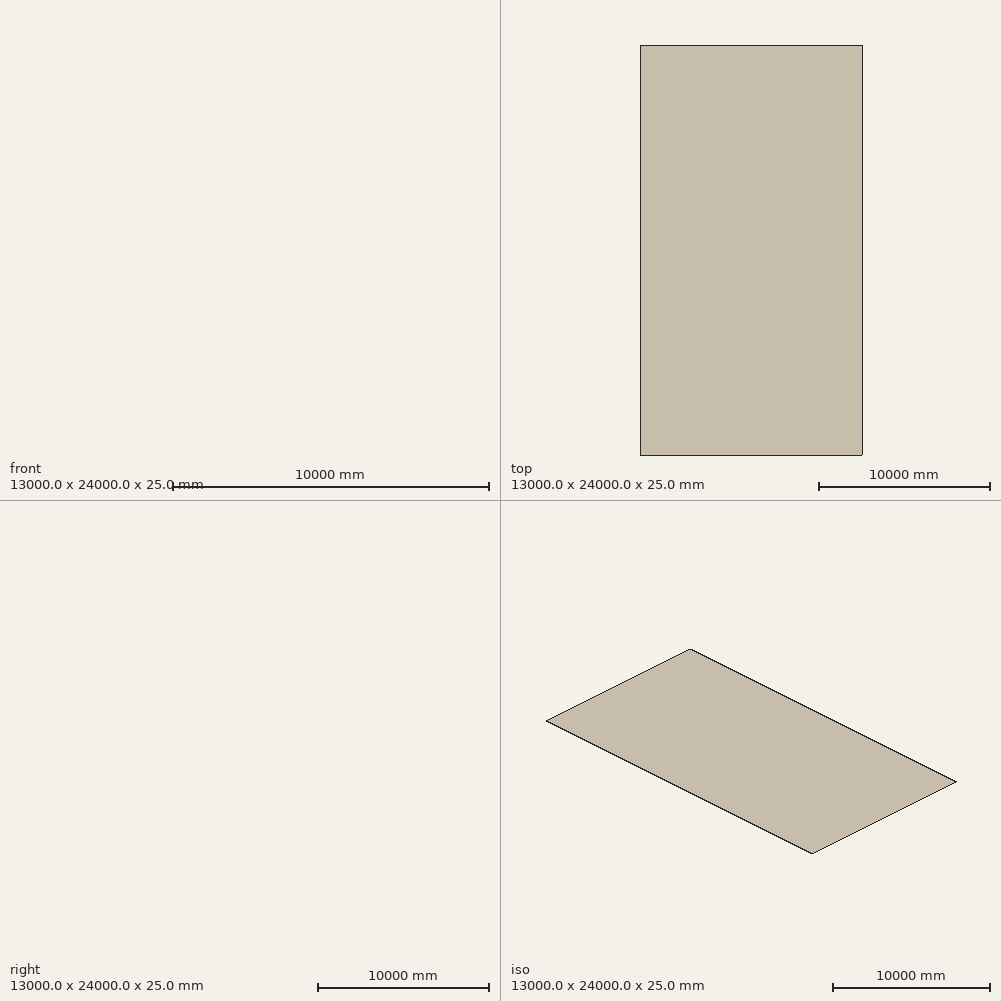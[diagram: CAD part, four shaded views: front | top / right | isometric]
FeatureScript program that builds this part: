
annotation { "Feature Type Name" : "Feature", "Feature Type Description" : "" }
export const myFeature = defineFeature(function(context is Context, id is Id, definition is map)
    precondition{}
    {
        {
            var Q0;
            Q0=qCreatedBy(makeId("Top.planeOp"),FACE);
            var sketch = newSketch(context, id + "F0", { "sketchPlane" : qUnion([Q0])});
            skLineSegment(sketch, "E0.bottom", {"start": v(6500, -12000) * mm, "end": v(-6500, -12000) * mm});
            skLineSegment(sketch, "E0.top", {"start": v(6500, 12000) * mm, "end": v(-6500, 12000) * mm});
            skLineSegment(sketch, "E0.left", {"start": v(6500, -12000) * mm, "end": v(6500, 12000) * mm});
            skLineSegment(sketch, "E0.right", {"start": v(-6500, -12000) * mm, "end": v(-6500, 12000) * mm});
            skPoint(sketch, "E0.middle", {"position": v(0, 0) * mm});
            skSolve(sketch);
        }
        {
            var Q0;
            Q0 = qSketchRegion(id + "F0", true);
            extrude(context, id + "F1", {"entities" : qUnion([Q0]), "depth" : 25 * mm});
        }
    });
